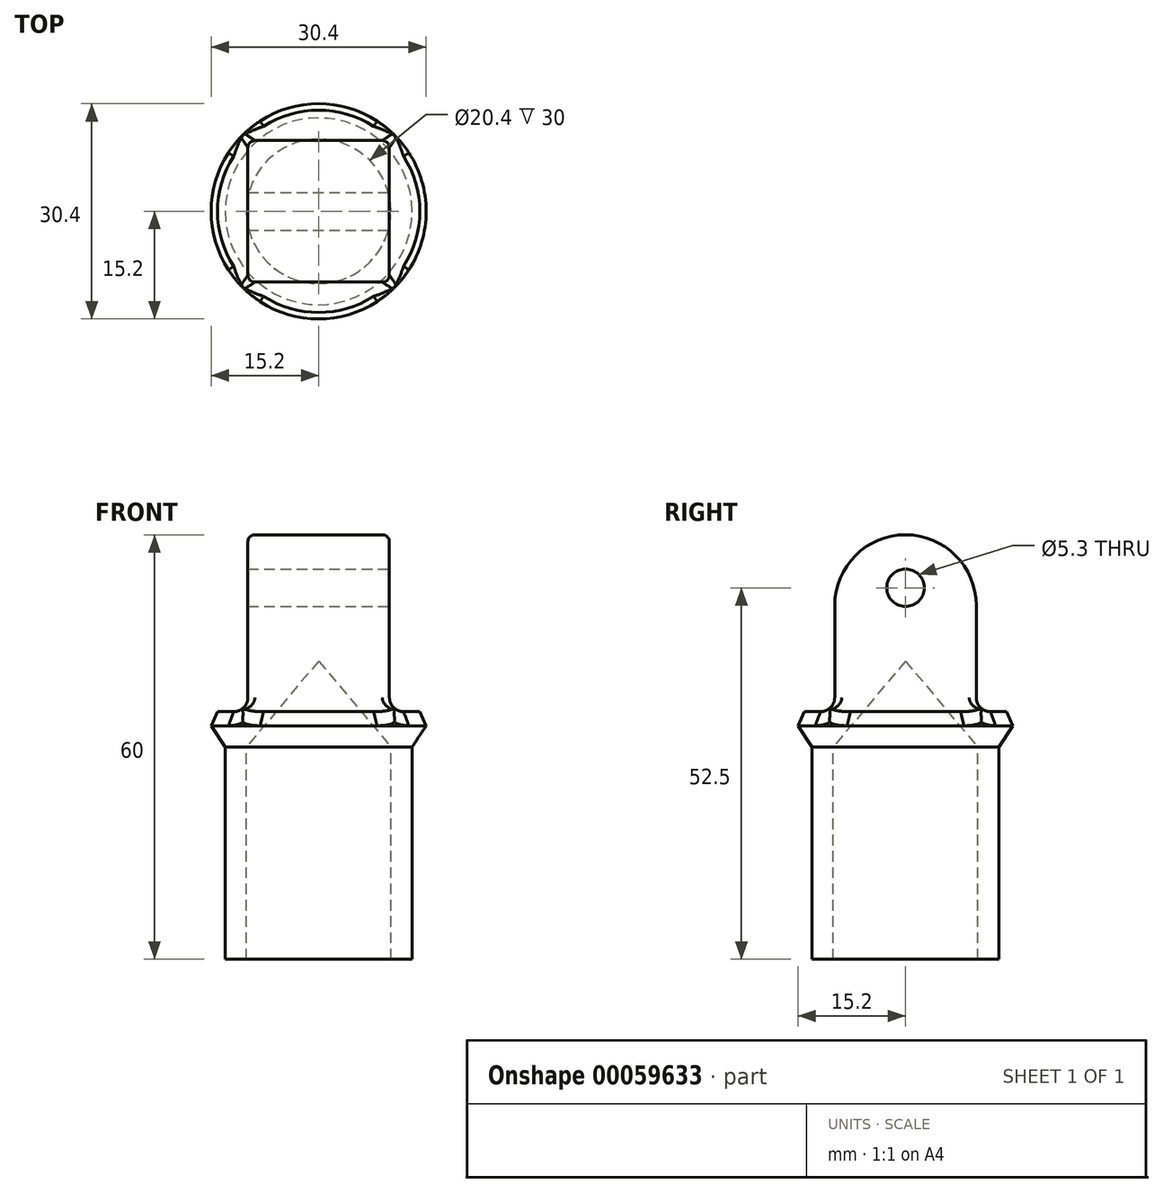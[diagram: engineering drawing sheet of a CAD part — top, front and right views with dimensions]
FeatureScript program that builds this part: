
annotation { "Feature Type Name" : "Feature", "Feature Type Description" : "" }
export const myFeature = defineFeature(function(context is Context, id is Id, definition is map)
    precondition{}
    {
        {
            var Q0;
            Q0=qCreatedBy(makeId("Top.planeOp"),FACE);
            var sketch = newSketch(context, id + "F0", { "sketchPlane" : qUnion([Q0])});
            skCircle(sketch, "E0", {"center": v(0, 0) * mm, "radius": 10.2 * mm});
            skCircle(sketch, "E1", {"center": v(0, 0) * mm, "radius": 13.2 * mm});
            skCircle(sketch, "E2", {"center": v(0, 0) * mm, "radius": 15.2 * mm});
            skLineSegment(sketch, "E3.rect.bottom", {"start": v(10, 10) * mm, "end": v(-10, 10) * mm});
            skLineSegment(sketch, "E3.rect.top", {"start": v(10, -10) * mm, "end": v(-10, -10) * mm});
            skLineSegment(sketch, "E3.rect.left", {"start": v(10, 10) * mm, "end": v(10, -10) * mm});
            skLineSegment(sketch, "E3.rect.right", {"start": v(-10, 10) * mm, "end": v(-10, -10) * mm});
            skSolve(sketch);
        }
        {
            var Q0;
            Q0=makeQuery(id+"F0.imprint","IMPRINT",FACE,{"disambiguationData":[TD([[makeQuery(id+"F0.imprint","IMPRINT",EDGE,{"derivedFrom":sQuery(id+"F0.wireOp",EDGE,"E2")}),1.0]])]});
            var Q1;
            {var subQ0=sQuery(id+"F0.wireOp",EDGE,"E3.rect.bottom");var subQ1=sQuery(id+"F0.wireOp",EDGE,"E0");var subQ2=makeQuery(id+"F0.imprint","INTERSECT",VERTEX,{"disambiguationData":[OD(0.0)],"derivedFrom":[subQ1,subQ0]});Q1=makeQuery(id+"F0.imprint","IMPRINT",FACE,{"disambiguationData":[TD([[makeQuery(id+"F0.imprint","IMPRINT",EDGE,{"disambiguationData":[TD([[subQ2,1.0]])],"derivedFrom":subQ1}),-1.0]])]});}
            var Q2;
            {var subQ0=sQuery(id+"F0.wireOp",EDGE,"E3.rect.bottom");var subQ1=sQuery(id+"F0.wireOp",EDGE,"E0");var subQ2=makeQuery(id+"F0.imprint","INTERSECT",VERTEX,{"disambiguationData":[OD(0.0)],"derivedFrom":[subQ1,subQ0]});Q2=makeQuery(id+"F0.imprint","IMPRINT",FACE,{"disambiguationData":[TD([[makeQuery(id+"F0.imprint","IMPRINT",EDGE,{"disambiguationData":[TD([[subQ2,-1.0]])],"derivedFrom":subQ1}),-1.0]])]});}
            var Q3;
            {var subQ0=sQuery(id+"F0.wireOp",EDGE,"E3.rect.bottom");var subQ1=sQuery(id+"F0.wireOp",EDGE,"E0");var subQ2=makeQuery(id+"F0.imprint","INTERSECT",VERTEX,{"disambiguationData":[OD(1.0)],"derivedFrom":[subQ1,subQ0]});Q3=makeQuery(id+"F0.imprint","IMPRINT",FACE,{"disambiguationData":[TD([[makeQuery(id+"F0.imprint","IMPRINT",EDGE,{"disambiguationData":[TD([[subQ2,-1.0]])],"derivedFrom":subQ1}),-1.0]])]});}
            var Q4;
            {var subQ0=sQuery(id+"F0.wireOp",EDGE,"E3.rect.right");var subQ1=sQuery(id+"F0.wireOp",EDGE,"E0");var subQ2=makeQuery(id+"F0.imprint","INTERSECT",VERTEX,{"disambiguationData":[OD(0.0)],"derivedFrom":[subQ1,subQ0]});Q4=makeQuery(id+"F0.imprint","IMPRINT",FACE,{"disambiguationData":[TD([[makeQuery(id+"F0.imprint","IMPRINT",EDGE,{"disambiguationData":[TD([[subQ2,-1.0]])],"derivedFrom":subQ1}),-1.0]])]});}
            var Q5;
            {var subQ0=sQuery(id+"F0.wireOp",EDGE,"E3.rect.right");var subQ1=sQuery(id+"F0.wireOp",EDGE,"E0");var subQ2=makeQuery(id+"F0.imprint","INTERSECT",VERTEX,{"disambiguationData":[OD(1.0)],"derivedFrom":[subQ1,subQ0]});Q5=makeQuery(id+"F0.imprint","IMPRINT",FACE,{"disambiguationData":[TD([[makeQuery(id+"F0.imprint","IMPRINT",EDGE,{"disambiguationData":[TD([[subQ2,-1.0]])],"derivedFrom":subQ1}),-1.0]])]});}
            var Q6;
            {var subQ0=sQuery(id+"F0.wireOp",EDGE,"E3.rect.top");var subQ1=sQuery(id+"F0.wireOp",EDGE,"E0");var subQ2=makeQuery(id+"F0.imprint","INTERSECT",VERTEX,{"disambiguationData":[OD(0.0)],"derivedFrom":[subQ1,subQ0]});Q6=makeQuery(id+"F0.imprint","IMPRINT",FACE,{"disambiguationData":[TD([[makeQuery(id+"F0.imprint","IMPRINT",EDGE,{"disambiguationData":[TD([[subQ2,-1.0]])],"derivedFrom":subQ1}),-1.0]])]});}
            var Q7;
            {var subQ0=sQuery(id+"F0.wireOp",EDGE,"E3.rect.top");var subQ1=sQuery(id+"F0.wireOp",EDGE,"E0");var subQ2=makeQuery(id+"F0.imprint","INTERSECT",VERTEX,{"disambiguationData":[OD(1.0)],"derivedFrom":[subQ1,subQ0]});Q7=makeQuery(id+"F0.imprint","IMPRINT",FACE,{"disambiguationData":[TD([[makeQuery(id+"F0.imprint","IMPRINT",EDGE,{"disambiguationData":[TD([[subQ2,-1.0]])],"derivedFrom":subQ1}),-1.0]])]});}
            var Q8;
            {var subQ0=sQuery(id+"F0.wireOp",EDGE,"E3.rect.left");var subQ1=sQuery(id+"F0.wireOp",EDGE,"E0");var subQ2=makeQuery(id+"F0.imprint","INTERSECT",VERTEX,{"disambiguationData":[OD(0.0)],"derivedFrom":[subQ1,subQ0]});Q8=makeQuery(id+"F0.imprint","IMPRINT",FACE,{"disambiguationData":[TD([[makeQuery(id+"F0.imprint","IMPRINT",EDGE,{"disambiguationData":[TD([[subQ2,1.0]])],"derivedFrom":subQ1}),-1.0]])]});}
            var Q9;
            {var subQ1=sQuery(id+"F0.wireOp",EDGE,"E0");var subQ8=sQuery(id+"F0.wireOp",EDGE,"E3.rect.bottom");var subQ12=makeQuery(id+"F0.imprint","INTERSECT",VERTEX,{"disambiguationData":[OD(0.0)],"derivedFrom":[subQ1,subQ8]});Q9=makeQuery(id+"F0.imprint","IMPRINT",FACE,{"disambiguationData":[TD([[makeQuery(id+"F0.imprint","IMPRINT",EDGE,{"disambiguationData":[TD([[subQ12,1.0]])],"derivedFrom":subQ1}),1.0]])]});}
            var Q10;
            {var subQ0=sQuery(id+"F0.wireOp",EDGE,"E3.rect.bottom");var subQ1=sQuery(id+"F0.wireOp",EDGE,"E1");var subQ2=makeQuery(id+"F0.imprint","INTERSECT",VERTEX,{"disambiguationData":[OD(1.0)],"derivedFrom":[subQ1,subQ0]});Q10=makeQuery(id+"F0.imprint","IMPRINT",FACE,{"disambiguationData":[TD([[makeQuery(id+"F0.imprint","IMPRINT",EDGE,{"disambiguationData":[TD([[subQ2,-1.0]])],"derivedFrom":subQ1}),-1.0]])]});}
            var Q11;
            {var subQ0=sQuery(id+"F0.wireOp",EDGE,"E3.rect.right");var subQ1=sQuery(id+"F0.wireOp",EDGE,"E1");var subQ2=makeQuery(id+"F0.imprint","INTERSECT",VERTEX,{"disambiguationData":[OD(1.0)],"derivedFrom":[subQ1,subQ0]});Q11=makeQuery(id+"F0.imprint","IMPRINT",FACE,{"disambiguationData":[TD([[makeQuery(id+"F0.imprint","IMPRINT",EDGE,{"disambiguationData":[TD([[subQ2,-1.0]])],"derivedFrom":subQ1}),-1.0]])]});}
            var Q12;
            {var subQ0=sQuery(id+"F0.wireOp",EDGE,"E3.rect.top");var subQ1=sQuery(id+"F0.wireOp",EDGE,"E1");var subQ2=makeQuery(id+"F0.imprint","INTERSECT",VERTEX,{"disambiguationData":[OD(1.0)],"derivedFrom":[subQ1,subQ0]});Q12=makeQuery(id+"F0.imprint","IMPRINT",FACE,{"disambiguationData":[TD([[makeQuery(id+"F0.imprint","IMPRINT",EDGE,{"disambiguationData":[TD([[subQ2,-1.0]])],"derivedFrom":subQ1}),-1.0]])]});}
            var Q13;
            {var subQ0=sQuery(id+"F0.wireOp",EDGE,"E3.rect.bottom");var subQ1=sQuery(id+"F0.wireOp",EDGE,"E1");var subQ2=makeQuery(id+"F0.imprint","INTERSECT",VERTEX,{"disambiguationData":[OD(0.0)],"derivedFrom":[subQ1,subQ0]});Q13=makeQuery(id+"F0.imprint","IMPRINT",FACE,{"disambiguationData":[TD([[makeQuery(id+"F0.imprint","IMPRINT",EDGE,{"disambiguationData":[TD([[subQ2,1.0]])],"derivedFrom":subQ1}),-1.0]])]});}
            var Q14;
            {var subQ0=sQuery(id+"F0.wireOp",EDGE,"E3.rect.left");var subQ1=sQuery(id+"F0.wireOp",EDGE,"E0");var subQ2=makeQuery(id+"F0.imprint","INTERSECT",VERTEX,{"disambiguationData":[OD(0.0)],"derivedFrom":[subQ1,subQ0]});Q14=makeQuery(id+"F0.imprint","IMPRINT",FACE,{"disambiguationData":[TD([[makeQuery(id+"F0.imprint","IMPRINT",EDGE,{"disambiguationData":[TD([[subQ2,1.0]])],"derivedFrom":subQ1}),1.0]])]});}
            var Q15;
            {var subQ0=sQuery(id+"F0.wireOp",EDGE,"E3.rect.bottom");var subQ1=sQuery(id+"F0.wireOp",EDGE,"E0");var subQ2=makeQuery(id+"F0.imprint","INTERSECT",VERTEX,{"disambiguationData":[OD(0.0)],"derivedFrom":[subQ1,subQ0]});Q15=makeQuery(id+"F0.imprint","IMPRINT",FACE,{"disambiguationData":[TD([[makeQuery(id+"F0.imprint","IMPRINT",EDGE,{"disambiguationData":[TD([[subQ2,-1.0]])],"derivedFrom":subQ1}),1.0]])]});}
            var Q16;
            {var subQ0=sQuery(id+"F0.wireOp",EDGE,"E3.rect.right");var subQ1=sQuery(id+"F0.wireOp",EDGE,"E0");var subQ2=makeQuery(id+"F0.imprint","INTERSECT",VERTEX,{"disambiguationData":[OD(0.0)],"derivedFrom":[subQ1,subQ0]});Q16=makeQuery(id+"F0.imprint","IMPRINT",FACE,{"disambiguationData":[TD([[makeQuery(id+"F0.imprint","IMPRINT",EDGE,{"disambiguationData":[TD([[subQ2,-1.0]])],"derivedFrom":subQ1}),1.0]])]});}
            var Q17;
            {var subQ0=sQuery(id+"F0.wireOp",EDGE,"E3.rect.top");var subQ1=sQuery(id+"F0.wireOp",EDGE,"E0");var subQ2=makeQuery(id+"F0.imprint","INTERSECT",VERTEX,{"disambiguationData":[OD(0.0)],"derivedFrom":[subQ1,subQ0]});Q17=makeQuery(id+"F0.imprint","IMPRINT",FACE,{"disambiguationData":[TD([[makeQuery(id+"F0.imprint","IMPRINT",EDGE,{"disambiguationData":[TD([[subQ2,-1.0]])],"derivedFrom":subQ1}),1.0]])]});}
            extrude(context, id + "F1", {"entities" : qUnion([Q0, Q1, Q2, Q3, Q4, Q5, Q6, Q7, Q8, Q9, Q10, Q11, Q12, Q13, Q14, Q15, Q16, Q17]), "depth" : 5 * mm});
        }
        {
            var Q0;
            {var subQ0=sQuery(id+"F0.wireOp",EDGE,"E1");var subQ1=makeQuery(id+"F0.imprint","INTERSECT",VERTEX,{"derivedFrom":[subQ0,sQuery(id+"F0.wireOp",EDGE,"1477c99b-9f6a-404b-9834-1aa7f952072c.rect.left")]});Q0=makeQuery(id+"F0.imprint","IMPRINT",FACE,{"disambiguationData":[TD([[makeQuery(id+"F0.imprint","IMPRINT",EDGE,{"disambiguationData":[TD([[subQ1,1.0]])],"derivedFrom":subQ0}),1.0]])]});}
            var Q1;
            {var subQ0=sQuery(id+"F0.wireOp",EDGE,"a9ac88e0-aa1a-4711-8ff9-0c26e18d78a5.rect.right");var subQ1=sQuery(id+"F0.wireOp",EDGE,"E0");var subQ2=makeQuery(id+"F0.imprint","INTERSECT",VERTEX,{"derivedFrom":[subQ1,subQ0]});Q1=makeQuery(id+"F0.imprint","IMPRINT",FACE,{"disambiguationData":[TD([[makeQuery(id+"F0.imprint","IMPRINT",EDGE,{"disambiguationData":[TD([[subQ2,-1.0]])],"derivedFrom":subQ1}),-1.0]])]});}
            var Q2;
            {var subQ0=sQuery(id+"F0.wireOp",EDGE,"E1");var subQ1=makeQuery(id+"F0.imprint","INTERSECT",VERTEX,{"derivedFrom":[subQ0,sQuery(id+"F0.wireOp",EDGE,"1477c99b-9f6a-404b-9834-1aa7f952072c.rect.top")]});Q2=makeQuery(id+"F0.imprint","IMPRINT",FACE,{"disambiguationData":[TD([[makeQuery(id+"F0.imprint","IMPRINT",EDGE,{"disambiguationData":[TD([[subQ1,1.0]])],"derivedFrom":subQ0}),1.0]])]});}
            var Q3;
            {var subQ0=sQuery(id+"F0.wireOp",EDGE,"a9ac88e0-aa1a-4711-8ff9-0c26e18d78a5.rect.left");var subQ1=sQuery(id+"F0.wireOp",EDGE,"E0");var subQ2=makeQuery(id+"F0.imprint","INTERSECT",VERTEX,{"derivedFrom":[subQ1,subQ0]});Q3=makeQuery(id+"F0.imprint","IMPRINT",FACE,{"disambiguationData":[TD([[makeQuery(id+"F0.imprint","IMPRINT",EDGE,{"disambiguationData":[TD([[subQ2,1.0]])],"derivedFrom":subQ1}),-1.0]])]});}
            var Q4;
            {var subQ0=sQuery(id+"F0.wireOp",EDGE,"E1");var subQ1=makeQuery(id+"F0.imprint","INTERSECT",VERTEX,{"derivedFrom":[subQ0,sQuery(id+"F0.wireOp",EDGE,"1477c99b-9f6a-404b-9834-1aa7f952072c.rect.right")]});Q4=makeQuery(id+"F0.imprint","IMPRINT",FACE,{"disambiguationData":[TD([[makeQuery(id+"F0.imprint","IMPRINT",EDGE,{"disambiguationData":[TD([[subQ1,-1.0]])],"derivedFrom":subQ0}),1.0]])]});}
            var Q5;
            {var subQ0=sQuery(id+"F0.wireOp",EDGE,"a9ac88e0-aa1a-4711-8ff9-0c26e18d78a5.rect.bottom");var subQ1=sQuery(id+"F0.wireOp",EDGE,"E0");var subQ2=makeQuery(id+"F0.imprint","INTERSECT",VERTEX,{"derivedFrom":[subQ1,subQ0]});Q5=makeQuery(id+"F0.imprint","IMPRINT",FACE,{"disambiguationData":[TD([[makeQuery(id+"F0.imprint","IMPRINT",EDGE,{"disambiguationData":[TD([[subQ2,1.0]])],"derivedFrom":subQ1}),-1.0]])]});}
            var Q6;
            {var subQ0=sQuery(id+"F0.wireOp",EDGE,"E1");var subQ1=makeQuery(id+"F0.imprint","INTERSECT",VERTEX,{"derivedFrom":[subQ0,sQuery(id+"F0.wireOp",EDGE,"1477c99b-9f6a-404b-9834-1aa7f952072c.rect.bottom")]});Q6=makeQuery(id+"F0.imprint","IMPRINT",FACE,{"disambiguationData":[TD([[makeQuery(id+"F0.imprint","IMPRINT",EDGE,{"disambiguationData":[TD([[subQ1,1.0]])],"derivedFrom":subQ0}),1.0]])]});}
            var Q7;
            {var subQ0=sQuery(id+"F0.wireOp",EDGE,"a9ac88e0-aa1a-4711-8ff9-0c26e18d78a5.rect.bottom");var subQ1=sQuery(id+"F0.wireOp",EDGE,"E0");var subQ2=makeQuery(id+"F0.imprint","INTERSECT",VERTEX,{"derivedFrom":[subQ1,subQ0]});Q7=makeQuery(id+"F0.imprint","IMPRINT",FACE,{"disambiguationData":[TD([[makeQuery(id+"F0.imprint","IMPRINT",EDGE,{"disambiguationData":[TD([[subQ2,-1.0]])],"derivedFrom":subQ1}),-1.0]])]});}
            extrude(context, id + "F2", {"entities" : qUnion([Q0, Q1, Q2, Q3, Q4, Q5, Q6, Q7]), "operationType" : NewBodyOperationType.ADD, "oppositeDirection" : true, "depth" : 30 * mm});
        }
        {
            var Q0;
            {var subQ0=sQuery(id+"F0.wireOp",EDGE,"E3.rect.bottom");var subQ1=sQuery(id+"F0.wireOp",EDGE,"E1");var subQ2=makeQuery(id+"F0.imprint","INTERSECT",VERTEX,{"disambiguationData":[OD(1.0)],"derivedFrom":[subQ1,subQ0]});Q0=makeQuery(id+"F0.imprint","IMPRINT",FACE,{"disambiguationData":[TD([[makeQuery(id+"F0.imprint","IMPRINT",EDGE,{"disambiguationData":[TD([[subQ2,-1.0]])],"derivedFrom":subQ1}),-1.0]])]});}
            var Q1;
            {var subQ0=sQuery(id+"F0.wireOp",EDGE,"E3.rect.bottom");var subQ1=sQuery(id+"F0.wireOp",EDGE,"E0");var subQ2=makeQuery(id+"F0.imprint","INTERSECT",VERTEX,{"disambiguationData":[OD(1.0)],"derivedFrom":[subQ1,subQ0]});Q1=makeQuery(id+"F0.imprint","IMPRINT",FACE,{"disambiguationData":[TD([[makeQuery(id+"F0.imprint","IMPRINT",EDGE,{"disambiguationData":[TD([[subQ2,-1.0]])],"derivedFrom":subQ1}),-1.0]])]});}
            var Q2;
            {var subQ0=sQuery(id+"F0.wireOp",EDGE,"E3.rect.bottom");var subQ1=sQuery(id+"F0.wireOp",EDGE,"E0");var subQ2=makeQuery(id+"F0.imprint","INTERSECT",VERTEX,{"disambiguationData":[OD(0.0)],"derivedFrom":[subQ1,subQ0]});Q2=makeQuery(id+"F0.imprint","IMPRINT",FACE,{"disambiguationData":[TD([[makeQuery(id+"F0.imprint","IMPRINT",EDGE,{"disambiguationData":[TD([[subQ2,1.0]])],"derivedFrom":subQ1}),-1.0]])]});}
            var Q3;
            {var subQ1=sQuery(id+"F0.wireOp",EDGE,"E0");var subQ8=sQuery(id+"F0.wireOp",EDGE,"E3.rect.bottom");var subQ12=makeQuery(id+"F0.imprint","INTERSECT",VERTEX,{"disambiguationData":[OD(0.0)],"derivedFrom":[subQ1,subQ8]});Q3=makeQuery(id+"F0.imprint","IMPRINT",FACE,{"disambiguationData":[TD([[makeQuery(id+"F0.imprint","IMPRINT",EDGE,{"disambiguationData":[TD([[subQ12,1.0]])],"derivedFrom":subQ1}),1.0]])]});}
            var Q4;
            {var subQ0=sQuery(id+"F0.wireOp",EDGE,"E3.rect.bottom");var subQ1=sQuery(id+"F0.wireOp",EDGE,"E1");var subQ2=makeQuery(id+"F0.imprint","INTERSECT",VERTEX,{"disambiguationData":[OD(0.0)],"derivedFrom":[subQ1,subQ0]});Q4=makeQuery(id+"F0.imprint","IMPRINT",FACE,{"disambiguationData":[TD([[makeQuery(id+"F0.imprint","IMPRINT",EDGE,{"disambiguationData":[TD([[subQ2,1.0]])],"derivedFrom":subQ1}),-1.0]])]});}
            var Q5;
            {var subQ0=sQuery(id+"F0.wireOp",EDGE,"E3.rect.right");var subQ1=sQuery(id+"F0.wireOp",EDGE,"E0");var subQ2=makeQuery(id+"F0.imprint","INTERSECT",VERTEX,{"disambiguationData":[OD(1.0)],"derivedFrom":[subQ1,subQ0]});Q5=makeQuery(id+"F0.imprint","IMPRINT",FACE,{"disambiguationData":[TD([[makeQuery(id+"F0.imprint","IMPRINT",EDGE,{"disambiguationData":[TD([[subQ2,-1.0]])],"derivedFrom":subQ1}),-1.0]])]});}
            var Q6;
            {var subQ0=sQuery(id+"F0.wireOp",EDGE,"E3.rect.right");var subQ1=sQuery(id+"F0.wireOp",EDGE,"E1");var subQ2=makeQuery(id+"F0.imprint","INTERSECT",VERTEX,{"disambiguationData":[OD(1.0)],"derivedFrom":[subQ1,subQ0]});Q6=makeQuery(id+"F0.imprint","IMPRINT",FACE,{"disambiguationData":[TD([[makeQuery(id+"F0.imprint","IMPRINT",EDGE,{"disambiguationData":[TD([[subQ2,-1.0]])],"derivedFrom":subQ1}),-1.0]])]});}
            var Q7;
            {var subQ0=sQuery(id+"F0.wireOp",EDGE,"E3.rect.top");var subQ1=sQuery(id+"F0.wireOp",EDGE,"E0");var subQ2=makeQuery(id+"F0.imprint","INTERSECT",VERTEX,{"disambiguationData":[OD(1.0)],"derivedFrom":[subQ1,subQ0]});Q7=makeQuery(id+"F0.imprint","IMPRINT",FACE,{"disambiguationData":[TD([[makeQuery(id+"F0.imprint","IMPRINT",EDGE,{"disambiguationData":[TD([[subQ2,-1.0]])],"derivedFrom":subQ1}),-1.0]])]});}
            var Q8;
            {var subQ0=sQuery(id+"F0.wireOp",EDGE,"E3.rect.top");var subQ1=sQuery(id+"F0.wireOp",EDGE,"E1");var subQ2=makeQuery(id+"F0.imprint","INTERSECT",VERTEX,{"disambiguationData":[OD(1.0)],"derivedFrom":[subQ1,subQ0]});Q8=makeQuery(id+"F0.imprint","IMPRINT",FACE,{"disambiguationData":[TD([[makeQuery(id+"F0.imprint","IMPRINT",EDGE,{"disambiguationData":[TD([[subQ2,-1.0]])],"derivedFrom":subQ1}),-1.0]])]});}
            var Q9;
            Q9=sQuery(id+"F0.wireOp",EDGE,"a9ac88e0-aa1a-4711-8ff9-0c26e18d78a5.rect.bottom");
            var Q10;
            Q10=sQuery(id+"F0.wireOp",EDGE,"a9ac88e0-aa1a-4711-8ff9-0c26e18d78a5.rect.right");
            var Q11;
            Q11=sQuery(id+"F0.wireOp",EDGE,"a9ac88e0-aa1a-4711-8ff9-0c26e18d78a5.rect.top");
            var Q12;
            Q12=sQuery(id+"F0.wireOp",EDGE,"a9ac88e0-aa1a-4711-8ff9-0c26e18d78a5.rect.left");
            extrude(context, id + "F3", {"entities" : qUnion([Q0, Q1, Q2, Q3, Q4, Q5, Q6, Q7, Q8]), "operationType" : NewBodyOperationType.ADD, "surfaceEntities" : qUnion([Q9, Q10, Q11, Q12]), "depth" : 30 * mm});
        }
        {
            var Q0;
            Q0=makeQuery(id+"F3.opExtrude","SWEPT_FACE",FACE,{"disambiguationData":[OSD([sQuery(id+"F0.wireOp",EDGE,"E3.rect.left")])]});
            var sketch = newSketch(context, id + "F4", { "sketchPlane" : qUnion([Q0])});
            skLineSegment(sketch, "E4", {"start": v(-10, 30) * mm, "end": v(10, 15) * mm});
            skLineSegment(sketch, "E5", {"start": v(10, 30) * mm, "end": v(-10, 15) * mm});
            skPoint(sketch, "E6", {"position": v(0, 22.5) * mm});
            skSolve(sketch);
        }
        {
            var Q0;
            Q0=sQuery(id+"F4.wireOp",VERTEX,"E6");
            var Q1;
            Q1=makeQuery(id+"F1.opExtrude","SWEPT_BODY",BODY,{"disambiguationData":[OSD([sQuery(id+"F0.wireOp",EDGE,"E2")])]});
            hole(context, id + "F5", {"style" : HoleStyle.SIMPLE, "holeDiameter" : 5.3 * mm, "endStyle" : HoleEndStyle.THROUGH, "locations" : qUnion([Q0]), "scope" : qUnion([Q1])});
        }
        {
            var Q0;
            Q0=makeQuery(id+"F3.boolean.opBoolean","INTERSECT",EDGE,{"derivedFrom":[makeQuery(id+"F1.opExtrude","CAP_FACE",FACE,{"disambiguationData":[OSD([sQuery(id+"F0.wireOp",EDGE,"E2")])],"isStart":false}),makeQuery(id+"F3.opExtrude","SWEPT_FACE",FACE,{"disambiguationData":[OSD([sQuery(id+"F0.wireOp",EDGE,"E3.rect.top")])]})]});
            var Q1;
            Q1=makeQuery(id+"F3.boolean.opBoolean","INTERSECT",EDGE,{"derivedFrom":[makeQuery(id+"F1.opExtrude","CAP_FACE",FACE,{"disambiguationData":[OSD([sQuery(id+"F0.wireOp",EDGE,"E2")])],"isStart":false}),makeQuery(id+"F3.opExtrude","SWEPT_FACE",FACE,{"disambiguationData":[OSD([sQuery(id+"F0.wireOp",EDGE,"E3.rect.left")])]})]});
            var Q2;
            Q2=makeQuery(id+"F3.boolean.opBoolean","INTERSECT",EDGE,{"derivedFrom":[makeQuery(id+"F1.opExtrude","CAP_FACE",FACE,{"disambiguationData":[OSD([sQuery(id+"F0.wireOp",EDGE,"E2")])],"isStart":false}),makeQuery(id+"F3.opExtrude","SWEPT_FACE",FACE,{"disambiguationData":[OSD([sQuery(id+"F0.wireOp",EDGE,"E3.rect.bottom")])]})]});
            var Q3;
            Q3=makeQuery(id+"F3.boolean.opBoolean","INTERSECT",EDGE,{"derivedFrom":[makeQuery(id+"F1.opExtrude","CAP_FACE",FACE,{"disambiguationData":[OSD([sQuery(id+"F0.wireOp",EDGE,"E2")])],"isStart":false}),makeQuery(id+"F3.opExtrude","SWEPT_FACE",FACE,{"disambiguationData":[OSD([sQuery(id+"F0.wireOp",EDGE,"E3.rect.right")])]})]});
            fillet(context, id + "F6", {"entities" : qUnion([Q0, Q1, Q2, Q3]), "radius" : 2 * mm, "allowEdgeOverflow" : false});
        }
        {
            var Q0;
            Q0=makeQuery(id+"F1.opExtrude","CAP_EDGE",EDGE,{"disambiguationData":[OSD([sQuery(id+"F0.wireOp",EDGE,"E2")])],"isStart":true});
            chamfer(context, id + "F7", {"entities" : qUnion([Q0]), "chamferType" : ChamferType.TWO_OFFSETS, "width1" : 3 * mm, "oppositeDirection" : false, "width2" : 2 * mm, "tangentPropagation" : true});
        }
        {
            var Q0;
            Q0=makeQuery(id+"F1.opExtrude","CAP_EDGE",EDGE,{"disambiguationData":[OSD([sQuery(id+"F0.wireOp",EDGE,"E2")])],"isStart":false});
            chamfer(context, id + "F8", {"entities" : qUnion([Q0]), "chamferType" : ChamferType.TWO_OFFSETS, "width1" : 0.9 * mm, "oppositeDirection" : false, "width2" : 2 * mm, "tangentPropagation" : true});
        }
        {
            var Q0;
            Q0=makeQuery(id+"F3.opExtrude","CAP_EDGE",EDGE,{"disambiguationData":[OSD([sQuery(id+"F0.wireOp",EDGE,"E3.rect.top")])],"isStart":false});
            var Q1;
            Q1=makeQuery(id+"F3.opExtrude","CAP_EDGE",EDGE,{"disambiguationData":[OSD([sQuery(id+"F0.wireOp",EDGE,"E3.rect.bottom")])],"isStart":false});
            fillet(context, id + "F9", {"entities" : qUnion([Q0, Q1]), "radius" : 10 * mm, "tangentPropagation" : true, "allowEdgeOverflow" : false});
        }
        {
            var Q0;
            Q0=makeQuery(id+"F9.opFillet","BLEND_EDGE",EDGE,{"blendedFrom":[makeQuery(id+"F3.opExtrude","CAP_EDGE",EDGE,{"disambiguationData":[OSD([sQuery(id+"F0.wireOp",EDGE,"E3.rect.bottom")])],"isStart":false}),makeQuery(id+"F3.opExtrude","SWEPT_FACE",FACE,{"disambiguationData":[OSD([sQuery(id+"F0.wireOp",EDGE,"E3.rect.right")])]})],"blendedInto":[makeQuery(id+"F3.opExtrude","SWEPT_FACE",FACE,{"disambiguationData":[OSD([sQuery(id+"F0.wireOp",EDGE,"E3.rect.right")])]})]});
            var Q1;
            Q1=makeQuery(id+"F3.opExtrude","SWEPT_EDGE",EDGE,{"disambiguationData":[OSD([sQuery(id+"F0.wireOp",EDGE,"E3.rect.top"),sQuery(id+"F0.wireOp",EDGE,"E3.rect.right")])]});
            var Q2;
            Q2=makeQuery(id+"F9.opFillet","BLEND_EDGE",EDGE,{"blendedFrom":[makeQuery(id+"F3.opExtrude","CAP_EDGE",EDGE,{"disambiguationData":[OSD([sQuery(id+"F0.wireOp",EDGE,"E3.rect.bottom")])],"isStart":false}),makeQuery(id+"F3.opExtrude","SWEPT_FACE",FACE,{"disambiguationData":[OSD([sQuery(id+"F0.wireOp",EDGE,"E3.rect.left")])]})],"blendedInto":[makeQuery(id+"F3.opExtrude","SWEPT_FACE",FACE,{"disambiguationData":[OSD([sQuery(id+"F0.wireOp",EDGE,"E3.rect.left")])]})]});
            fillet(context, id + "F10", {"entities" : qUnion([Q0, Q1, Q2]), "radius" : 1 * mm, "tangentPropagation" : true, "allowEdgeOverflow" : false});
        }
        {
            var Q0;
            Q0=makeQuery(id+"F2.boolean.opBoolean","SPLIT",FACE,{"disambiguationData":[TD([makeQuery(id+"F2.opExtrude","SWEPT_FACE",FACE,{"disambiguationData":[OSD([sQuery(id+"F0.wireOp",EDGE,"E0")])]})])],"derivedFrom":makeQuery(id+"F1.opExtrude","CAP_FACE",FACE,{"disambiguationData":[OSD([sQuery(id+"F0.wireOp",EDGE,"E2")])],"isStart":true})});
            var sketch = newSketch(context, id + "F11", { "sketchPlane" : qUnion([Q0])});
            skCircle(sketch, "E7", {"center": v(0, 0) * mm, "radius": 10.2 * mm});
            skSolve(sketch);
        }
        {
            var Q0;
            Q0 = qSketchRegion(id + "F11", true);
            var Q1;
            Q1=makeQuery(id+"F11.imprint","IMPRINT",FACE,{"disambiguationData":[TD([[makeQuery(id+"F11.imprint","IMPRINT",EDGE,{"derivedFrom":sQuery(id+"F11.wireOp",EDGE,"E7")}),1.0]])]});
            extrude(context, id + "F12", {"entities" : qUnion([Q0, Q1]), "operationType" : NewBodyOperationType.REMOVE, "oppositeDirection" : true, "depth" : 14 * mm, "hasDraft" : true, "draftAngle" : 40 * degree, "draftPullDirection" : true});
        }
    });
